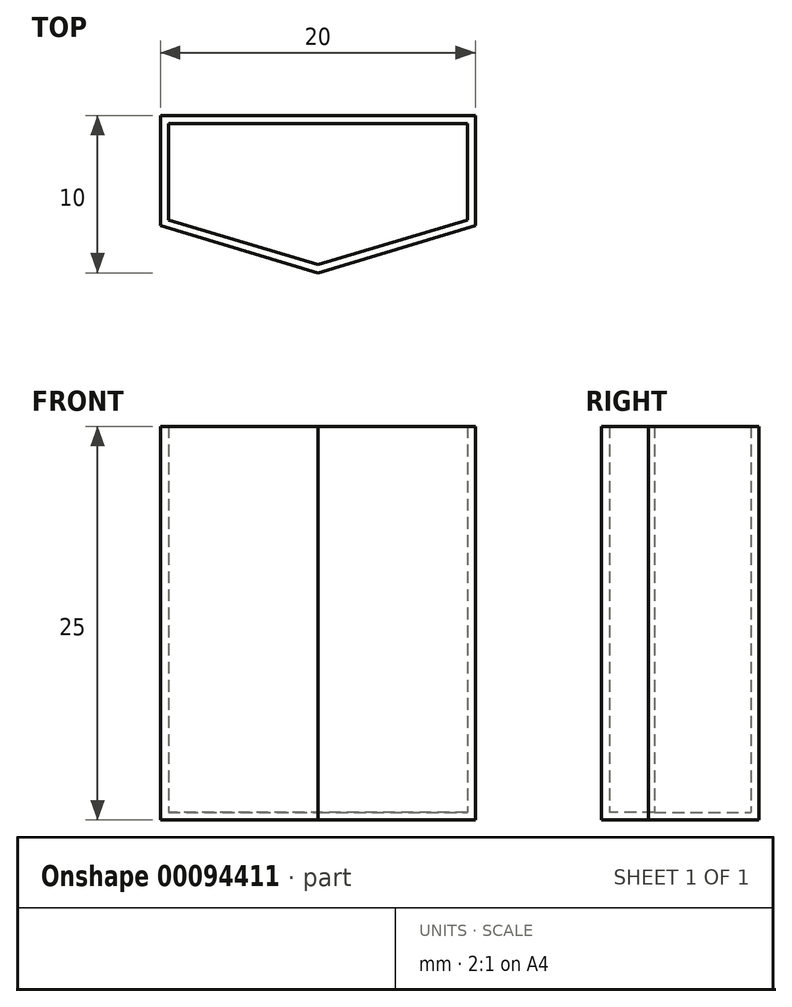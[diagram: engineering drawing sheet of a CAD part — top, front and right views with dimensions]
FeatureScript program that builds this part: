
annotation { "Feature Type Name" : "Feature", "Feature Type Description" : "" }
export const myFeature = defineFeature(function(context is Context, id is Id, definition is map)
    precondition{}
    {
        {
            var Q0;
            Q0=qCreatedBy(makeId("Top.planeOp"),FACE);
            var sketch = newSketch(context, id + "F0", { "sketchPlane" : qUnion([Q0])});
            skLineSegment(sketch, "E0", {"start": v(0, 0) * mm, "end": v(10, 3) * mm});
            skLineSegment(sketch, "E1", {"start": v(10, 3) * mm, "end": v(10, 10) * mm});
            skLineSegment(sketch, "E2", {"start": v(10, 10) * mm, "end": v(-10, 10) * mm});
            skLineSegment(sketch, "E3", {"start": v(-10, 10) * mm, "end": v(-10, 3) * mm});
            skLineSegment(sketch, "E4", {"start": v(-10, 3) * mm, "end": v(0, 0) * mm});
            skSolve(sketch);
        }
        {
            var Q0;
            Q0 = qSketchRegion(id + "F0", true);
            extrude(context, id + "F1", {"entities" : qUnion([Q0]), "endBound" : BoundingType.SYMMETRIC, "depth" : 25 * mm});
        }
        {
            var Q0;
            Q0=makeQuery(id+"F1.opExtrude","CAP_FACE",FACE,{"disambiguationData":[OSD([sQuery(id+"F0.wireOp",EDGE,"E0"),sQuery(id+"F0.wireOp",EDGE,"E1"),sQuery(id+"F0.wireOp",EDGE,"E2"),sQuery(id+"F0.wireOp",EDGE,"E3"),sQuery(id+"F0.wireOp",EDGE,"E4")])],"isStart":false});
            shell(context, id + "F2", {"entities" : qUnion([Q0]), "thickness" : 0.5 * mm});
        }
    });
